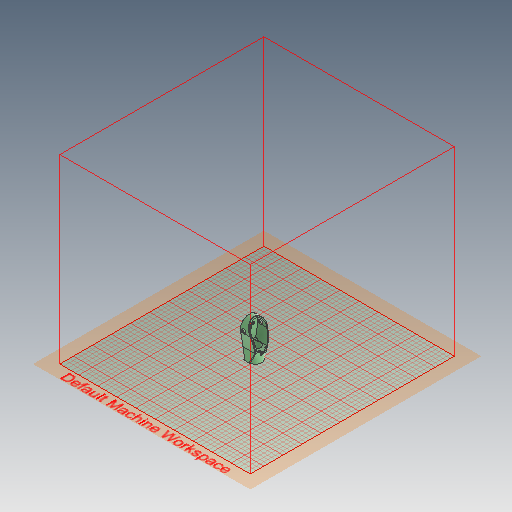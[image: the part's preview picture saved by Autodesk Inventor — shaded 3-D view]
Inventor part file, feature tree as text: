
AUTODESK INVENTOR PART (.ipt)
format: ipt  version: 2021 (Build 250183000, 183)  size: 2,821,120 bytes
history: native  units: mm
features: extrude x12, sketch x11, other x6, fillet x3, chamfer x3, loft x1
ambient origin geometry x8: Origin, YZ Plane, XZ Plane, XY Plane, X Axis, Y Axis, Z Axis, Center Point
bodies: Body1 (feature_tree)
feature tree (36):
  other  "Sólido1"
  extrude  "Extrusão1"  Depth=500.0mm
  extrude  "Extrusão2"  Depth=5.0mm TaperAngle=0.0deg
  extrude  "Extrusão4"  Depth=10.0mm TaperAngle=0.0deg
  extrude  "Extrusão3"  Depth=14.0mm
  other  "Plano de trabalho1"
  fillet  "Arredondamento1"  Radius=3.2mm
  loft  "Transição1"
  extrude  "Extrusão8"  Depth=11.0mm
  extrude  "Extrusão9"  TaperAngle=0.0deg  [1 undecoded]
  chamfer  "Chanfro1"  Distance=25.0mm
  extrude  "Extrusão7"  Depth=8.0mm
  extrude  "Extrusão12"  Depth=0.5mm TaperAngle=0.0deg
  extrude  "Extrusão10"  Depth=1.5mm
  chamfer  "Chanfro2"  Distance=47.189mm
  fillet  "Arredondamento2"  Radius=2.0mm
  extrude  "Extrusão11"  Depth=3.5mm TaperAngle=0.0deg
  fillet  "Arredondamento3"  Radius=1.0mm
  extrude  "Extrusão13"  Depth=3.5mm
  chamfer  "Chanfro3"  Distance=5.0mm
  extrude  "Extrusão14"  Depth=10.0mm
  sketch  "Esboço1"  dims[d0=40.0mm d3=500.0mm]
  sketch  "Esboço3"  dims[d4=28.5mm d5=0.0mm d7=5.0mm d9=25.5mm d10=0.0mm]
  sketch  "Esboço4"  dims[d12=10.0mm d13=25.0mm d14=0.0mm]
  other  "Contorno projetado1"
  sketch  "Esboço8"  dims[d17=30.005mm d18=0.0mm d29=14.0mm d43=3.2mm]
  sketch  "Esboço9"  dims[d45=36.0mm d46=28.0mm]
  other  "Arestas2"
  sketch  "Esboço10"  dims[d47=3.0mm d48=11.0mm]
  sketch  "Esboço11"  dims[d49=24.0mm d51=0.0mm d52=90.0deg d53=0.0mm d54=90.0deg d56=25.0mm d57=0.0mm]
  sketch  "Esboço13"  dims[d58=1.0mm d60=8.0mm]
  sketch  "Esboço14"  dims[d61=6.0mm d62=0.5mm d63=0.0mm]
  sketch  "Esboço15"  dims[d65=33.0mm d66=0.0mm d67=1.5mm d69=47.189mm d70=0.0mm d71=2.0mm]
  other  "Contorno projetado5"
  sketch  "Esboço16"  dims[d78=9.0mm d80=20.154mm d81=0.0mm d82=1.0mm d83=0.5mm d85=5.0mm d86=10.0mm d88=22.5mm d91=19.3mm d92=0.5mm d93=2.0mm d94=45.0deg d95=6.981317mm d96=1.0mm d97=4.0mm d98=0.0mm d99=2.999mm d100=2.0mm d101=45.0deg d102=12.5mm d103=0.0mm d104=3.5mm d105=4.0mm d106=0.0mm d107=5.0mm d108=0.2mm d109=0.0mm d110=2.3mm d111=2.0mm d112=45.0deg d59=0.5mm]
  other  "Projetar arestas de corte1"
note: 1 required parameter value undecoded (feature->parameter linkage not recoverable at this tier; creation-order binding heuristic only, values carry confidence <= 0.55)
